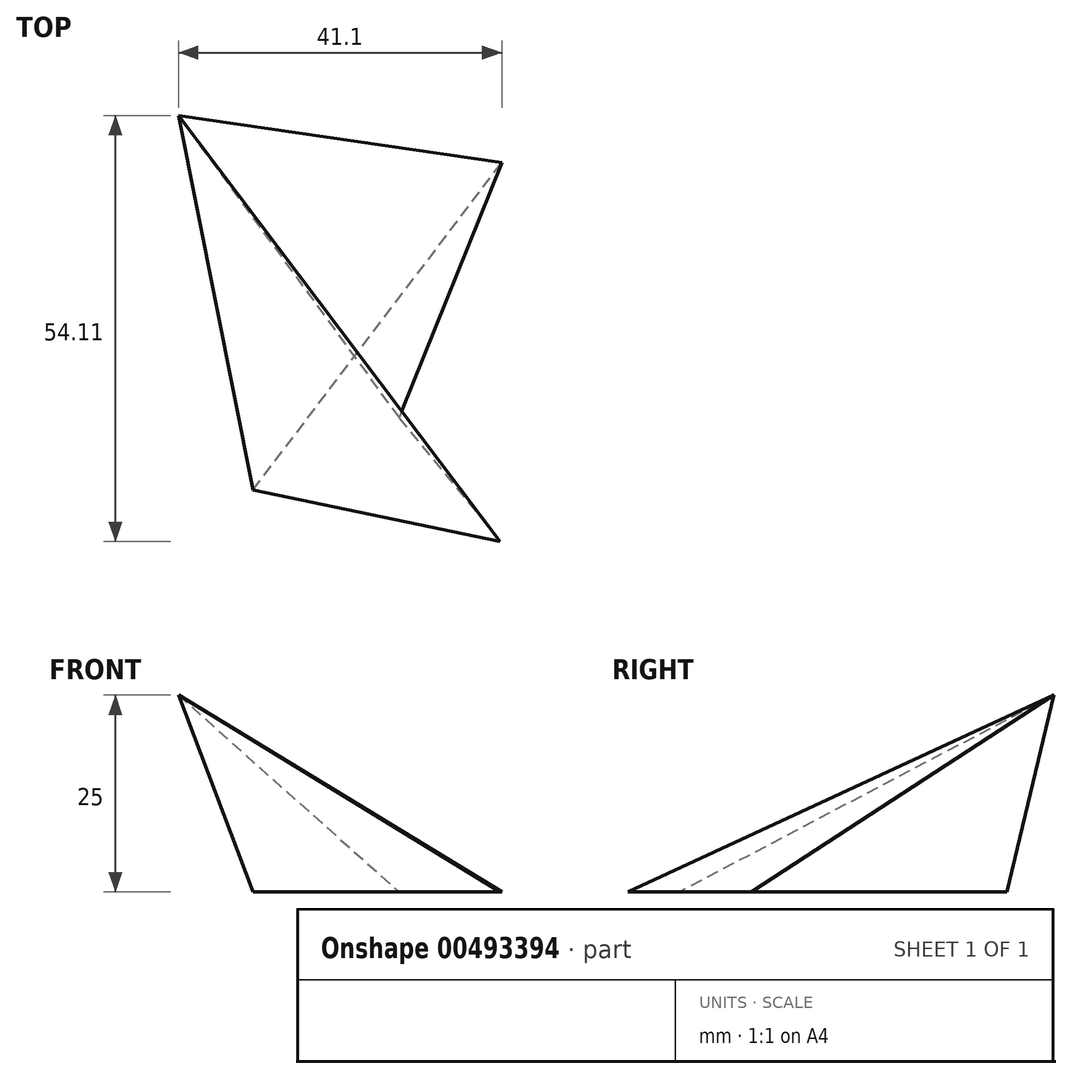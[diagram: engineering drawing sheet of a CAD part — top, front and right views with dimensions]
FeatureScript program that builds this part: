
annotation { "Feature Type Name" : "Feature", "Feature Type Description" : "" }
export const myFeature = defineFeature(function(context is Context, id is Id, definition is map)
    precondition{}
    {
        {
            var Q0;
            Q0=qCreatedBy(makeId("Top.planeOp"),FACE);
            var sketch = newSketch(context, id + "F0", { "sketchPlane" : qUnion([Q0])});
            skLineSegment(sketch, "E0", {"start": v(40.87, -54.11) * mm, "end": v(9.48, -47.56) * mm});
            skLineSegment(sketch, "E1", {"start": v(9.48, -47.56) * mm, "end": v(41.1, -5.95) * mm});
            skLineSegment(sketch, "E2", {"start": v(41.1, -5.95) * mm, "end": v(28.04, -38.4) * mm});
            skLineSegment(sketch, "E3", {"start": v(28.04, -38.4) * mm, "end": v(40.87, -54.11) * mm});
            skSolve(sketch);
        }
        {
            var Q0;
            Q0=qCreatedBy(makeId("Top.planeOp"),FACE);
            cPlane(context, id + "F1", {"entities" : qUnion([Q0]), "cplaneType" : CPlaneType.OFFSET, "offset" : 25 * mm, "width" : 150 * mm, "height" : 150 * mm});
        }
        {
            var Q0;
            Q0=qCreatedBy(id+"F1.planeOp",FACE);
            var sketch = newSketch(context, id + "F2", { "sketchPlane" : qUnion([Q0])});
            skPoint(sketch, "E4", {"position": v(0, 0) * mm});
            skSolve(sketch);
        }
        {
            var Q0;
            Q0=sQuery(id+"F2.wireOp",VERTEX,"E4");
            var Q1;
            Q1=makeQuery(id+"F0.imprint","IMPRINT",FACE,{"disambiguationData":[TD([[makeQuery(id+"F0.imprint","IMPRINT",EDGE,{"derivedFrom":sQuery(id+"F0.wireOp",EDGE,"E0")}),-1.0]])]});
            loft(context, id + "F3", {"sheetProfilesArray" : [{ "sheetProfileEntities" : qUnion([Q0]) }, { "sheetProfileEntities" : qUnion([Q1]) }]});
        }
    });
